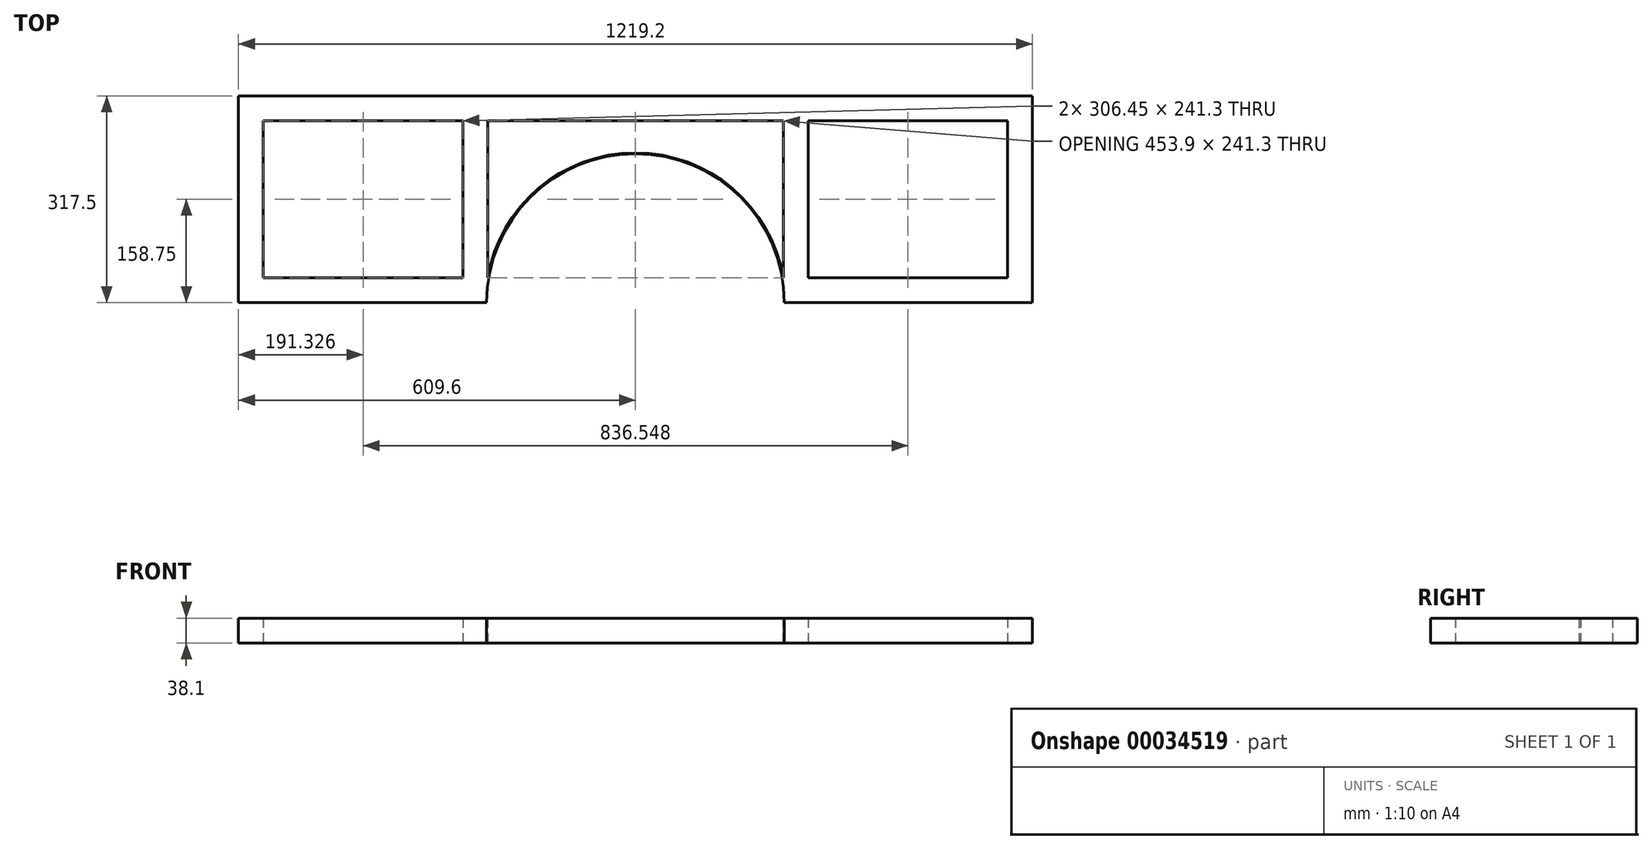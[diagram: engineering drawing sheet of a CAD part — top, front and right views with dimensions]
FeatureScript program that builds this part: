
annotation { "Feature Type Name" : "Feature", "Feature Type Description" : "" }
export const myFeature = defineFeature(function(context is Context, id is Id, definition is map)
    precondition{}
    {
        {
            var Q0;
            Q0=qCreatedBy(makeId("Top.planeOp"),FACE);
            var sketch = newSketch(context, id + "F0", { "sketchPlane" : qUnion([Q0])});
            skCircle(sketch, "E0", {"center": v(0, 0) * mm, "radius": 228.6 * mm});
            skSolve(sketch);
        }
        {
            var Q0;
            Q0=makeQuery(id+"F0.imprint","IMPRINT",FACE,{"disambiguationData":[TD([[makeQuery(id+"F0.imprint","IMPRINT",EDGE,{"derivedFrom":sQuery(id+"F0.wireOp",EDGE,"E0")}),1.0]])]});
            extrude(context, id + "F1", {"entities" : qUnion([Q0]), "endBound" : BoundingType.SYMMETRIC, "depth" : 4572 * mm});
        }
        {
            var Q0;
            Q0=qCreatedBy(makeId("Top.planeOp"),FACE);
            var sketch = newSketch(context, id + "F2", { "sketchPlane" : qUnion([Q0])});
            skCircle(sketch, "E1.0", {"center": v(0, 0) * mm, "radius": 226.95 * mm});
            skCircle(sketch, "E2.0", {"center": v(0, 0) * mm, "radius": 230.12 * mm});
            skLineSegment(sketch, "E3", {"start": v(0, 0) * mm, "end": v(0, 230.12) * mm});
            skLineSegment(sketch, "E4", {"start": v(0, 0) * mm, "end": v(-230.12, 0) * mm});
            skSolve(sketch);
        }
        {
            var Q0;
            {var subQ1=sQuery(id+"F2.wireOp",EDGE,"E1.0");var subQ5=sQuery(id+"F2.wireOp",EDGE,"E3");var subQ6=makeQuery(id+"F2.imprint","INTERSECT",VERTEX,{"derivedFrom":[subQ1,subQ5]});Q0=makeQuery(id+"F2.imprint","IMPRINT",FACE,{"disambiguationData":[TD([[makeQuery(id+"F2.imprint","IMPRINT",EDGE,{"disambiguationData":[TD([[subQ6,-1.0]])],"derivedFrom":subQ1}),-1.0]])]});}
            extrude(context, id + "F3", {"entities" : qUnion([Q0]), "operationType" : NewBodyOperationType.ADD, "depth" : 38.1 * mm});
        }
        {
            var Q0;
            Q0=makeQuery(id+"F1.opExtrude","SWEPT_BODY",BODY,{"disambiguationData":[OSD([sQuery(id+"F0.wireOp",EDGE,"E0")])]});
            var Q1;
            Q1=makeQuery(id+"F3.opExtrude","SWEPT_FACE",FACE,{"disambiguationData":[OSD([sQuery(id+"F2.wireOp",EDGE,"E3")])]});
            mirror(context, id + "F4", {"operationType" : NewBodyOperationType.ADD, "entities" : qUnion([Q0]), "mirrorPlane" : qUnion([Q1])});
        }
        {
            var Q0;
            Q0=qCreatedBy(makeId("Right.planeOp"),FACE);
            cPlane(context, id + "F5", {"entities" : qUnion([Q0]), "cplaneType" : CPlaneType.OFFSET, "offset" : 609.6 * mm, "width" : 152.4 * mm, "height" : 152.4 * mm});
        }
        {
            var Q0;
            Q0=qCreatedBy(id+"F5.planeOp",FACE);
            var sketch = newSketch(context, id + "F6", { "sketchPlane" : qUnion([Q0])});
            skLineSegment(sketch, "E5.bottom", {"start": v(0, 0) * mm, "end": v(38.1, 0) * mm});
            skLineSegment(sketch, "E5.top", {"start": v(0, 38.1) * mm, "end": v(38.1, 38.1) * mm});
            skLineSegment(sketch, "E5.left", {"start": v(0, 0) * mm, "end": v(0, 38.1) * mm});
            skLineSegment(sketch, "E5.right", {"start": v(38.1, 0) * mm, "end": v(38.1, 38.1) * mm});
            skSolve(sketch);
        }
        {
            var Q0;
            Q0 = qSketchRegion(id + "F6", true);
            extrude(context, id + "F7", {"entities" : qUnion([Q0]), "operationType" : NewBodyOperationType.ADD, "endBound" : BoundingType.UP_TO_NEXT, "oppositeDirection" : true, "depth" : 25.4 * mm});
        }
        {
            var Q0;
            Q0=makeQuery(id+"F7.opExtrude","SWEPT_FACE",FACE,{"disambiguationData":[OSD([sQuery(id+"F6.wireOp",EDGE,"E5.right")])]});
            var sketch = newSketch(context, id + "F8", { "sketchPlane" : qUnion([Q0])});
            skLineSegment(sketch, "E6.bottom", {"start": v(-609.6, 38.1) * mm, "end": v(-571.5, 38.1) * mm});
            skLineSegment(sketch, "E6.top", {"start": v(-609.6, 0) * mm, "end": v(-571.5, 0) * mm});
            skLineSegment(sketch, "E6.left", {"start": v(-609.6, 38.1) * mm, "end": v(-609.6, 0) * mm});
            skLineSegment(sketch, "E6.right", {"start": v(-571.5, 38.1) * mm, "end": v(-571.5, 0) * mm});
            skLineSegment(sketch, "E7.bottom", {"start": v(-226.95, 38.1) * mm, "end": v(-265.05, 38.1) * mm});
            skLineSegment(sketch, "E7.top", {"start": v(-226.95, 0) * mm, "end": v(-265.05, 0) * mm});
            skLineSegment(sketch, "E7.left", {"start": v(-226.95, 38.1) * mm, "end": v(-226.95, 0) * mm});
            skLineSegment(sketch, "E7.right", {"start": v(-265.05, 38.1) * mm, "end": v(-265.05, 0) * mm});
            skSolve(sketch);
        }
        {
            var Q0;
            Q0 = qSketchRegion(id + "F8", true);
            extrude(context, id + "F9", {"entities" : qUnion([Q0]), "operationType" : NewBodyOperationType.ADD, "depth" : 279.4 * mm});
        }
        {
            var Q0;
            Q0=makeQuery(id+"F9.opExtrude","CAP_FACE",FACE,{"disambiguationData":[OSD([sQuery(id+"F8.wireOp",EDGE,"E6.bottom"),sQuery(id+"F8.wireOp",EDGE,"E6.top"),sQuery(id+"F8.wireOp",EDGE,"E6.left"),sQuery(id+"F8.wireOp",EDGE,"E6.right")])],"isStart":false});
            var sketch = newSketch(context, id + "F10", { "sketchPlane" : qUnion([Q0])});
            skLineSegment(sketch, "E8.bottom", {"start": v(-609.6, 38.1) * mm, "end": v(0, 38.1) * mm});
            skLineSegment(sketch, "E8.top", {"start": v(-609.6, 0) * mm, "end": v(0, 0) * mm});
            skLineSegment(sketch, "E8.left", {"start": v(-609.6, 38.1) * mm, "end": v(-609.6, 0) * mm});
            skLineSegment(sketch, "E8.right", {"start": v(0, 38.1) * mm, "end": v(0, 0) * mm});
            skSolve(sketch);
        }
        {
            var Q0;
            {var subQ1=sQuery(id+"F10.wireOp",EDGE,"E8.right");Q0=makeQuery(id+"F10.imprint","IMPRINT",FACE,{"disambiguationData":[TD([[makeQuery(id+"F10.imprint","IMPRINT",EDGE,{"derivedFrom":subQ1}),-1.0]])]});}
            extrude(context, id + "F11", {"entities" : qUnion([Q0]), "operationType" : NewBodyOperationType.ADD, "oppositeDirection" : true, "depth" : 38.1 * mm});
        }
        {
            var Q0;
            {var subQ0=sQuery(id+"F8.wireOp",EDGE,"E6.right");Q0=makeQuery(id+"F11.boolean.opBoolean","MERGE",FACE,{"derivedFrom":[makeQuery(id+"F9.opExtrude","CAP_FACE",FACE,{"disambiguationData":[OSD([sQuery(id+"F8.wireOp",EDGE,"E6.bottom"),sQuery(id+"F8.wireOp",EDGE,"E6.top"),sQuery(id+"F8.wireOp",EDGE,"E6.left"),subQ0])],"isStart":false}),makeQuery(id+"F9.opExtrude","CAP_FACE",FACE,{"disambiguationData":[OSD([sQuery(id+"F8.wireOp",EDGE,"E7.bottom"),sQuery(id+"F8.wireOp",EDGE,"E7.top"),sQuery(id+"F8.wireOp",EDGE,"E7.left"),sQuery(id+"F8.wireOp",EDGE,"E7.right")])],"isStart":false}),makeQuery(id+"F11.opExtrude","CAP_FACE",FACE,{"disambiguationData":[OSD([subQ0,sQuery(id+"F10.wireOp",EDGE,"E8.bottom"),sQuery(id+"F10.wireOp",EDGE,"E8.top"),sQuery(id+"F10.wireOp",EDGE,"E8.right")])],"isStart":true})]});}
            var sketch = newSketch(context, id + "F12", { "sketchPlane" : qUnion([Q0])});
            skLineSegment(sketch, "E9.bottom", {"start": v(0, 38.1) * mm, "end": v(424.94, 38.1) * mm});
            skLineSegment(sketch, "E9.top", {"start": v(0, 0) * mm, "end": v(424.94, 0) * mm});
            skLineSegment(sketch, "E9.left", {"start": v(0, 38.1) * mm, "end": v(0, 0) * mm});
            skLineSegment(sketch, "E9.right", {"start": v(424.94, 38.1) * mm, "end": v(424.94, 0) * mm});
            skSolve(sketch);
        }
        {
            var Q0;
            Q0=makeQuery(id+"F12.imprint","IMPRINT",FACE,{"disambiguationData":[TD([[makeQuery(id+"F12.imprint","IMPRINT",EDGE,{"derivedFrom":sQuery(id+"F12.wireOp",EDGE,"E9.bottom")}),-1.0]])]});
            extrude(context, id + "F13", {"entities" : qUnion([Q0]), "operationType" : NewBodyOperationType.REMOVE, "endBound" : BoundingType.THROUGH_ALL, "oppositeDirection" : true, "depth" : 25.23 * mm});
        }
        {
            var Q0;
            Q0=makeQuery(id+"F1.opExtrude","CAP_FACE",FACE,{"disambiguationData":[OSD([sQuery(id+"F0.wireOp",EDGE,"E0")])],"isStart":false});
            var sketch = newSketch(context, id + "F14", { "sketchPlane" : qUnion([Q0])});
            skCircle(sketch, "E10", {"center": v(0, 0) * mm, "radius": 228.6 * mm});
            skSolve(sketch);
        }
        {
            var Q0;
            Q0=makeQuery(id+"F14.imprint","IMPRINT",FACE,{"disambiguationData":[TD([[makeQuery(id+"F14.imprint","IMPRINT",EDGE,{"derivedFrom":sQuery(id+"F14.wireOp",EDGE,"E10")}),1.0]])]});
            extrude(context, id + "F15", {"entities" : qUnion([Q0]), "operationType" : NewBodyOperationType.REMOVE, "oppositeDirection" : true, "depth" : 4572 * mm});
        }
        {
            var Q0;
            Q0=makeQuery(id+"F1.opExtrude","SWEPT_BODY",BODY,{"disambiguationData":[OSD([sQuery(id+"F0.wireOp",EDGE,"E0")])]});
            var Q1;
            Q1=makeQuery(id+"F11.opExtrude","SWEPT_FACE",FACE,{"disambiguationData":[OSD([sQuery(id+"F10.wireOp",EDGE,"E8.right")])]});
            mirror(context, id + "F16", {"operationType" : NewBodyOperationType.ADD, "entities" : qUnion([Q0]), "mirrorPlane" : qUnion([Q1])});
        }
    });
